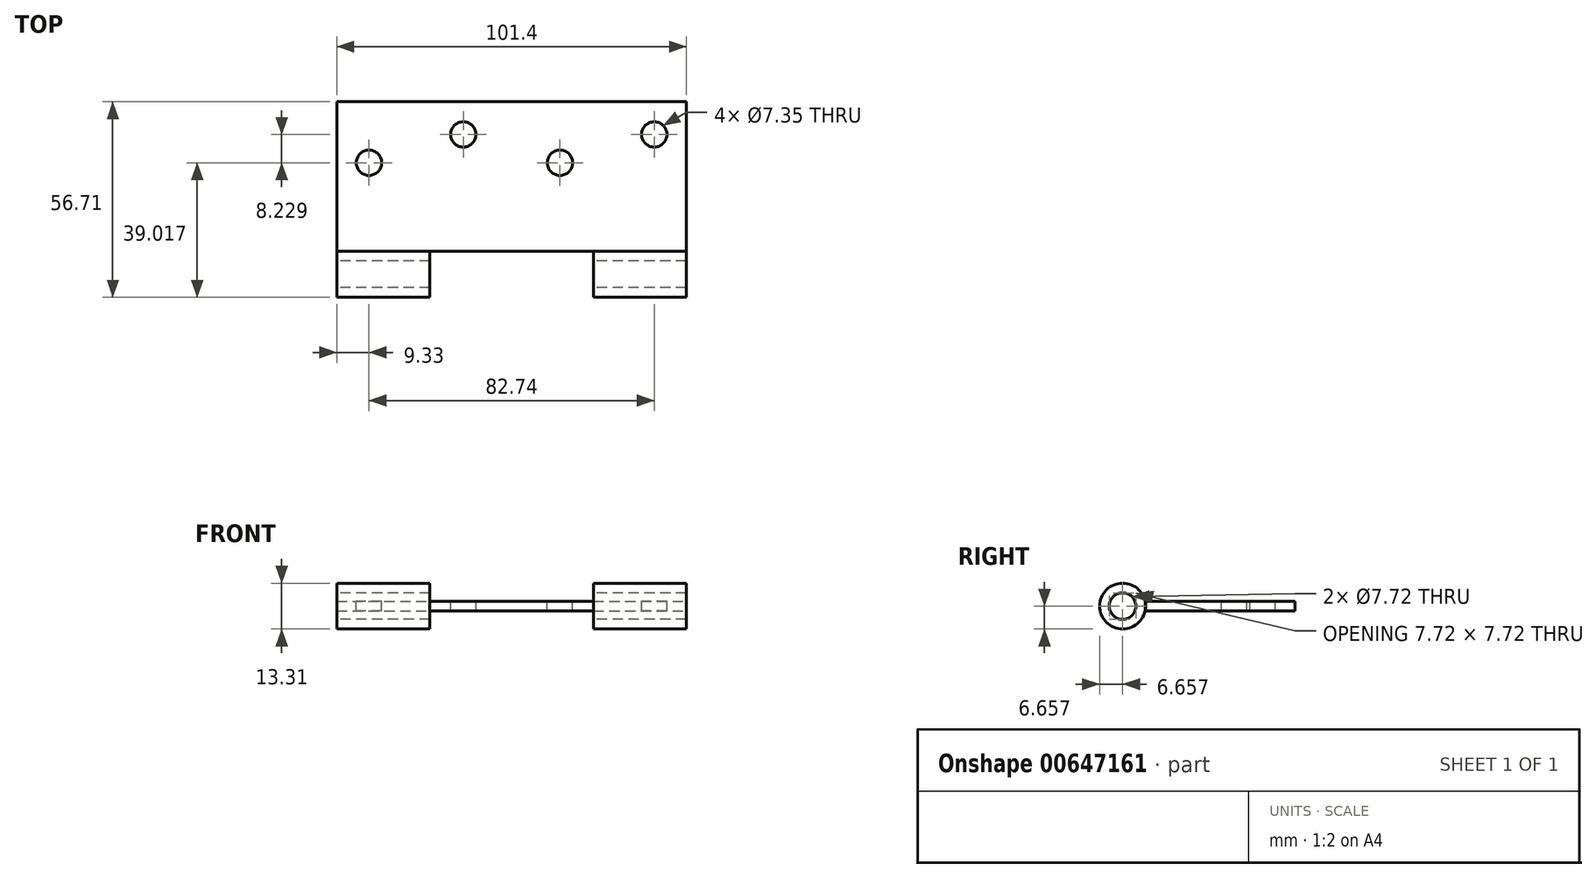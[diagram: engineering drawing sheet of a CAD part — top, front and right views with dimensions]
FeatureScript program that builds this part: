
annotation { "Feature Type Name" : "Feature", "Feature Type Description" : "" }
export const myFeature = defineFeature(function(context is Context, id is Id, definition is map)
    precondition{}
    {
        {
            var Q0;
            Q0=qCreatedBy(makeId("Top.planeOp"),FACE);
            var sketch = newSketch(context, id + "F0", { "sketchPlane" : qUnion([Q0])});
            skLineSegment(sketch, "E0.bottom", {"start": v(-50.7, 21.7) * mm, "end": v(50.7, 21.7) * mm});
            skLineSegment(sketch, "E0.top", {"start": v(-50.7, -21.7) * mm, "end": v(50.7, -21.7) * mm});
            skLineSegment(sketch, "E0.left", {"start": v(-50.7, 21.7) * mm, "end": v(-50.7, -21.7) * mm});
            skLineSegment(sketch, "E0.right", {"start": v(50.7, 21.7) * mm, "end": v(50.7, -21.7) * mm});
            skSolve(sketch);
        }
        {
            var Q0;
            Q0 = qSketchRegion(id + "F0", true);
            extrude(context, id + "F1", {"entities" : qUnion([Q0]), "depth" : 2.8 * mm, "offsetDistance" : 25.4 * mm});
        }
        {
            var Q0;
            Q0=makeQuery(id+"F1.opExtrude","SWEPT_FACE",FACE,{"disambiguationData":[OSD([sQuery(id+"F0.wireOp",EDGE,"E0.left")])]});
            var sketch = newSketch(context, id + "F2", { "sketchPlane" : qUnion([Q0])});
            skCircle(sketch, "E1", {"center": v(28.35, 1.4) * mm, "radius": 6.65 * mm});
            skPoint(sketch, "E1.centerSnap0", {"position": v(21.7, 1.4) * mm});
            skCircle(sketch, "E2.0", {"center": v(28.35, 1.4) * mm, "radius": 3.86 * mm});
            skSolve(sketch);
        }
        {
            var Q0;
            Q0 = qSketchRegion(id + "F2", true);
            extrude(context, id + "F3", {"entities" : qUnion([Q0]), "operationType" : NewBodyOperationType.ADD, "oppositeDirection" : true, "depth" : 101.4 * mm, "offsetDistance" : 25.4 * mm});
        }
        {
            var Q0;
            Q0=qCreatedBy(makeId("Right.planeOp"),FACE);
            var sketch = newSketch(context, id + "F4", { "sketchPlane" : qUnion([Q0])});
            skCircle(sketch, "E3.0", {"center": v(-28.35, 1.4) * mm, "radius": 6.65 * mm});
            skCircle(sketch, "E4.0", {"center": v(-28.35, 1.4) * mm, "radius": 3.86 * mm});
            skSolve(sketch);
        }
        {
            var Q0;
            Q0 = qSketchRegion(id + "F4", true);
            extrude(context, id + "F5", {"entities" : qUnion([Q0]), "operationType" : NewBodyOperationType.REMOVE, "depth" : 23.72 * mm, "offsetDistance" : 25.4 * mm, "hasSecondDirection" : true, "secondDirectionOppositeDirection" : true, "secondDirectionDepth" : 23.72 * mm});
        }
        {
            var Q0;
            Q0=makeQuery(id+"F1.opExtrude","CAP_FACE",FACE,{"disambiguationData":[OSD([sQuery(id+"F0.wireOp",EDGE,"E0.bottom"),sQuery(id+"F0.wireOp",EDGE,"E0.top"),sQuery(id+"F0.wireOp",EDGE,"E0.left"),sQuery(id+"F0.wireOp",EDGE,"E0.right")])],"isStart":false});
            var sketch = newSketch(context, id + "F6", { "sketchPlane" : qUnion([Q0])});
            skPoint(sketch, "E5", {"position": v(41.37, 12.24) * mm});
            skPoint(sketch, "E6", {"position": v(14.01, 4) * mm});
            skPoint(sketch, "E7", {"position": v(-14.01, 12.24) * mm});
            skPoint(sketch, "E8", {"position": v(-41.37, 4) * mm});
            skSolve(sketch);
        }
        {
            var Q0;
            Q0=sQuery(id+"F6.wireOp",VERTEX,"E5");
            var Q1;
            Q1=sQuery(id+"F6.wireOp",VERTEX,"E6");
            var Q2;
            Q2=sQuery(id+"F6.wireOp",VERTEX,"E7");
            var Q3;
            Q3=sQuery(id+"F6.wireOp",VERTEX,"E8");
            var Q4;
            Q4=makeQuery(id+"F1.opExtrude","SWEPT_BODY",BODY,{"disambiguationData":[OSD([sQuery(id+"F0.wireOp",EDGE,"E0.bottom"),sQuery(id+"F0.wireOp",EDGE,"E0.top"),sQuery(id+"F0.wireOp",EDGE,"E0.left"),sQuery(id+"F0.wireOp",EDGE,"E0.right")])]});
            hole(context, id + "F7", {"style" : HoleStyle.SIMPLE, "endStyle" : HoleEndStyle.BLIND, "holeDiameter" : 7.35 * mm, "majorDiameter" : 6.35 * mm, "holeDepth" : 12.7 * mm, "isTappedThrough" : true, "tappedDepth" : 12.7 * mm, "tapClearance" : 3, "locations" : qUnion([Q0, Q1, Q2, Q3]), "scope" : qUnion([Q4])});
        }
    });
